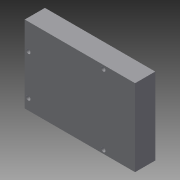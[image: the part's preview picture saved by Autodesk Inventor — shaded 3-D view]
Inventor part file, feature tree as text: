
AUTODESK INVENTOR PART (.ipt)
format: ipt  version: 2015 (Build 190159000, 159)  size: 89,088 bytes
history: native  units: mm
features: extrude x1, sketch x1
ambient origin geometry x8: Origin, YZ Plane, XZ Plane, XY Plane, X Axis, Y Axis, Z Axis, Center Point
bodies: Solid1 (feature_tree)
feature tree (2):
  extrude  "Extrusion1"  Depth=76.5mm
  sketch  "Sketch1"  dims[d0=53.4mm d2=76.5mm d3=3.0mm d4=3.0mm d5=3.0mm d6=3.0mm d7=2.5mm d8=7.5mm d9=28.0mm d10=2.5mm d11=52.0mm d12=2.5mm d13=52.0mm d14=14.0mm d15=0.0mm d16=2.5mm]
